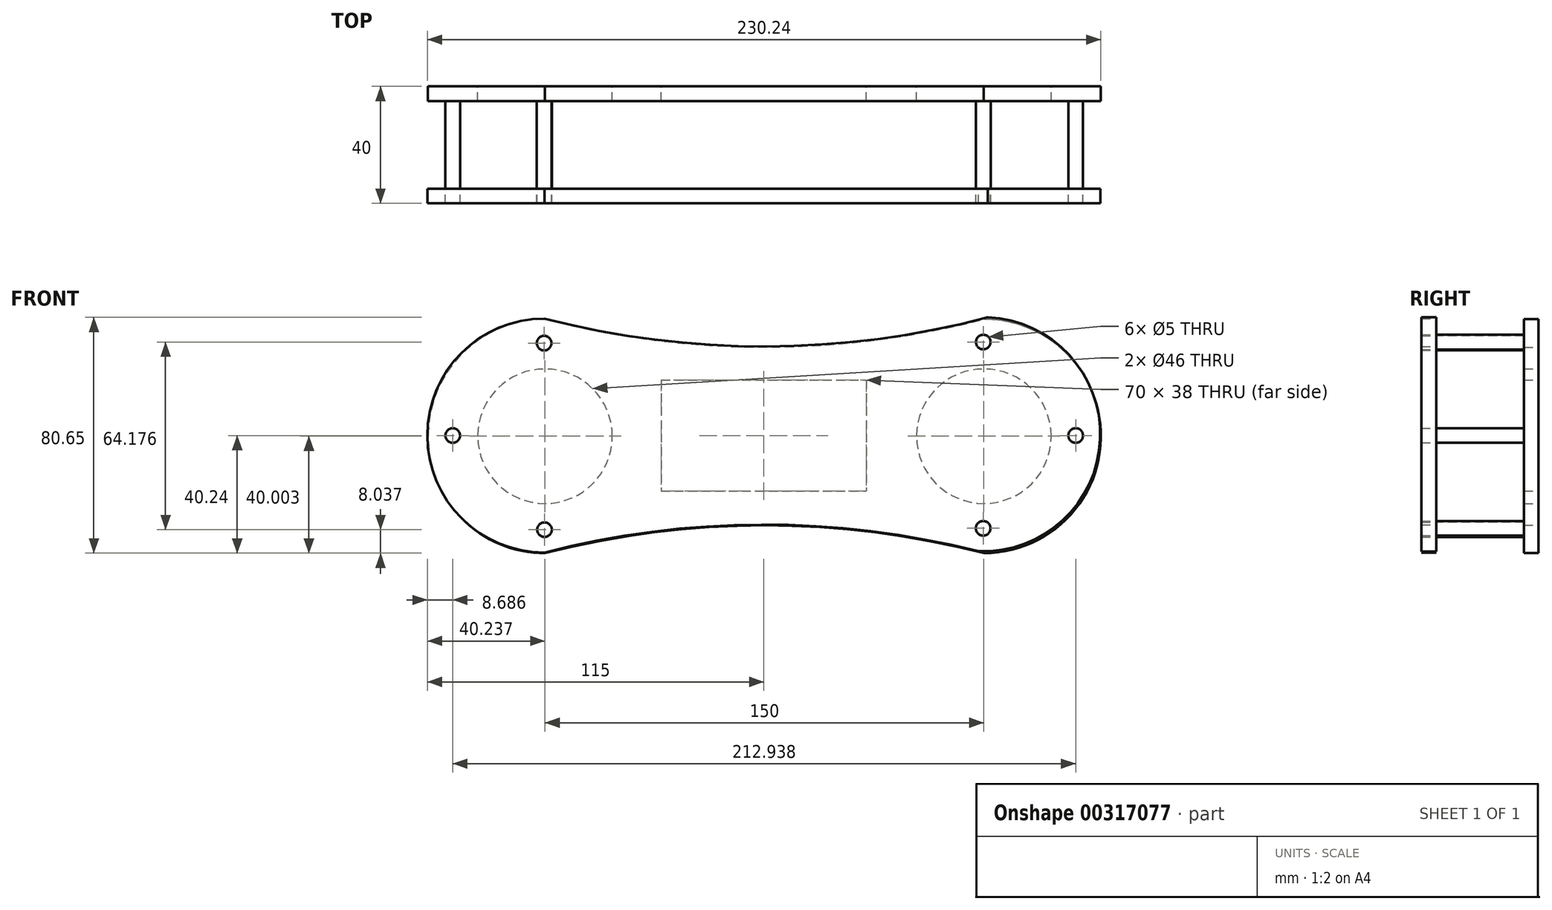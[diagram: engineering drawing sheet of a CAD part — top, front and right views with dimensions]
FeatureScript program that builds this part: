
annotation { "Feature Type Name" : "Feature", "Feature Type Description" : "" }
export const myFeature = defineFeature(function(context is Context, id is Id, definition is map)
    precondition{}
    {
        {
            var Q0;
            Q0=qCreatedBy(makeId("Front.planeOp"),FACE);
            var sketch = newSketch(context, id + "F0", { "sketchPlane" : qUnion([Q0])});
            skArc(sketch, "E0", {"start": v(75.24, -40.24) * mm, "mid": v(115.24, -0.24) * mm, "end": v(75.24, 39.76) * mm});
            skArc(sketch, "E1", {"start": v(-74.76, 39.76) * mm, "mid": v(-114.76, -0.24) * mm, "end": v(-74.76, -40.24) * mm});
            skArc(sketch, "E2", {"start": v(-74.76, 39.76) * mm, "mid": v(0.24, 30.24) * mm, "end": v(75.24, 39.76) * mm});
            skArc(sketch, "E3", {"start": v(75.24, -40.24) * mm, "mid": v(0.24, -30.71) * mm, "end": v(-74.76, -40.24) * mm});
            skCircle(sketch, "E4", {"center": v(75.24, -0.24) * mm, "radius": 23 * mm});
            skCircle(sketch, "E5", {"center": v(-74.76, -0.24) * mm, "radius": 23 * mm});
            skLineSegment(sketch, "E6.bottom", {"start": v(-35, 19) * mm, "end": v(35, 19) * mm});
            skLineSegment(sketch, "E6.top", {"start": v(-35, -19) * mm, "end": v(35, -19) * mm});
            skLineSegment(sketch, "E6.left", {"start": v(-35, 19) * mm, "end": v(-35, -19) * mm});
            skLineSegment(sketch, "E6.right", {"start": v(35, 19) * mm, "end": v(35, -19) * mm});
            skPoint(sketch, "E6.middle", {"position": v(0, 0) * mm});
            skSolve(sketch);
        }
        {
            var Q0;
            Q0=makeQuery(id+"F0.imprint","IMPRINT",FACE,{"disambiguationData":[TD([[makeQuery(id+"F0.imprint","IMPRINT",EDGE,{"derivedFrom":sQuery(id+"F0.wireOp",EDGE,"E0")}),1.0]])]});
            extrude(context, id + "F1", {"entities" : qUnion([Q0]), "depth" : 5 * mm});
        }
        {
            var Q0;
            Q0=qCreatedBy(makeId("Front.planeOp"),FACE);
            cPlane(context, id + "F2", {"entities" : qUnion([Q0]), "cplaneType" : CPlaneType.OFFSET, "offset" : 35 * mm, "width" : 150 * mm, "height" : 150 * mm});
        }
        {
            var Q0;
            Q0=qCreatedBy(id+"F2.planeOp",FACE);
            var sketch = newSketch(context, id + "F3", { "sketchPlane" : qUnion([Q0])});
            skArc(sketch, "E7", {"start": v(73.4, -39.6) * mm, "mid": v(114.98, -1.17) * mm, "end": v(76.56, 40.4) * mm});
            skArc(sketch, "E8", {"start": v(-75, 40) * mm, "mid": v(-115, 0) * mm, "end": v(-75, -40) * mm});
            skArc(sketch, "E9", {"start": v(-75, 40) * mm, "mid": v(0.8, 30.47) * mm, "end": v(76.56, 40.4) * mm});
            skArc(sketch, "E10", {"start": v(73.4, -39.6) * mm, "mid": v(-0.82, -30.47) * mm, "end": v(-75, -40) * mm});
            skCircle(sketch, "E11", {"center": v(75.03, 31.97) * mm, "radius": 2.5 * mm});
            skCircle(sketch, "E12", {"center": v(75, -31.73) * mm, "radius": 2.5 * mm});
            skCircle(sketch, "E13", {"center": v(-75.07, 31.6) * mm, "radius": 2.5 * mm});
            skCircle(sketch, "E14", {"center": v(-74.95, -32.2) * mm, "radius": 2.5 * mm});
            skCircle(sketch, "E15", {"center": v(-106.31, 0) * mm, "radius": 2.5 * mm});
            skCircle(sketch, "E16", {"center": v(106.62, 0) * mm, "radius": 2.5 * mm});
            skSolve(sketch);
        }
        {
            var Q0;
            Q0 = qSketchRegion(id + "F3", true);
            extrude(context, id + "F4", {"entities" : qUnion([Q0]), "depth" : 5 * mm});
        }
        {
            var Q0;
            Q0=makeQuery(id+"F3.imprint","IMPRINT",FACE,{"disambiguationData":[TD([[makeQuery(id+"F3.imprint","IMPRINT",EDGE,{"derivedFrom":sQuery(id+"F3.wireOp",EDGE,"E13")}),1.0]])]});
            var Q1;
            Q1=makeQuery(id+"F3.imprint","IMPRINT",FACE,{"disambiguationData":[TD([[makeQuery(id+"F3.imprint","IMPRINT",EDGE,{"derivedFrom":sQuery(id+"F3.wireOp",EDGE,"E15")}),1.0]])]});
            var Q2;
            Q2=makeQuery(id+"F3.imprint","IMPRINT",FACE,{"disambiguationData":[TD([[makeQuery(id+"F3.imprint","IMPRINT",EDGE,{"derivedFrom":sQuery(id+"F3.wireOp",EDGE,"E14")}),1.0]])]});
            var Q3;
            Q3=makeQuery(id+"F3.imprint","IMPRINT",FACE,{"disambiguationData":[TD([[makeQuery(id+"F3.imprint","IMPRINT",EDGE,{"derivedFrom":sQuery(id+"F3.wireOp",EDGE,"E11")}),1.0]])]});
            var Q4;
            Q4=makeQuery(id+"F3.imprint","IMPRINT",FACE,{"disambiguationData":[TD([[makeQuery(id+"F3.imprint","IMPRINT",EDGE,{"derivedFrom":sQuery(id+"F3.wireOp",EDGE,"E16")}),1.0]])]});
            var Q5;
            Q5=makeQuery(id+"F3.imprint","IMPRINT",FACE,{"disambiguationData":[TD([[makeQuery(id+"F3.imprint","IMPRINT",EDGE,{"derivedFrom":sQuery(id+"F3.wireOp",EDGE,"E12")}),1.0]])]});
            extrude(context, id + "F5", {"entities" : qUnion([Q0, Q1, Q2, Q3, Q4, Q5]), "operationType" : NewBodyOperationType.ADD, "oppositeDirection" : true, "depth" : 30 * mm});
        }
    });
